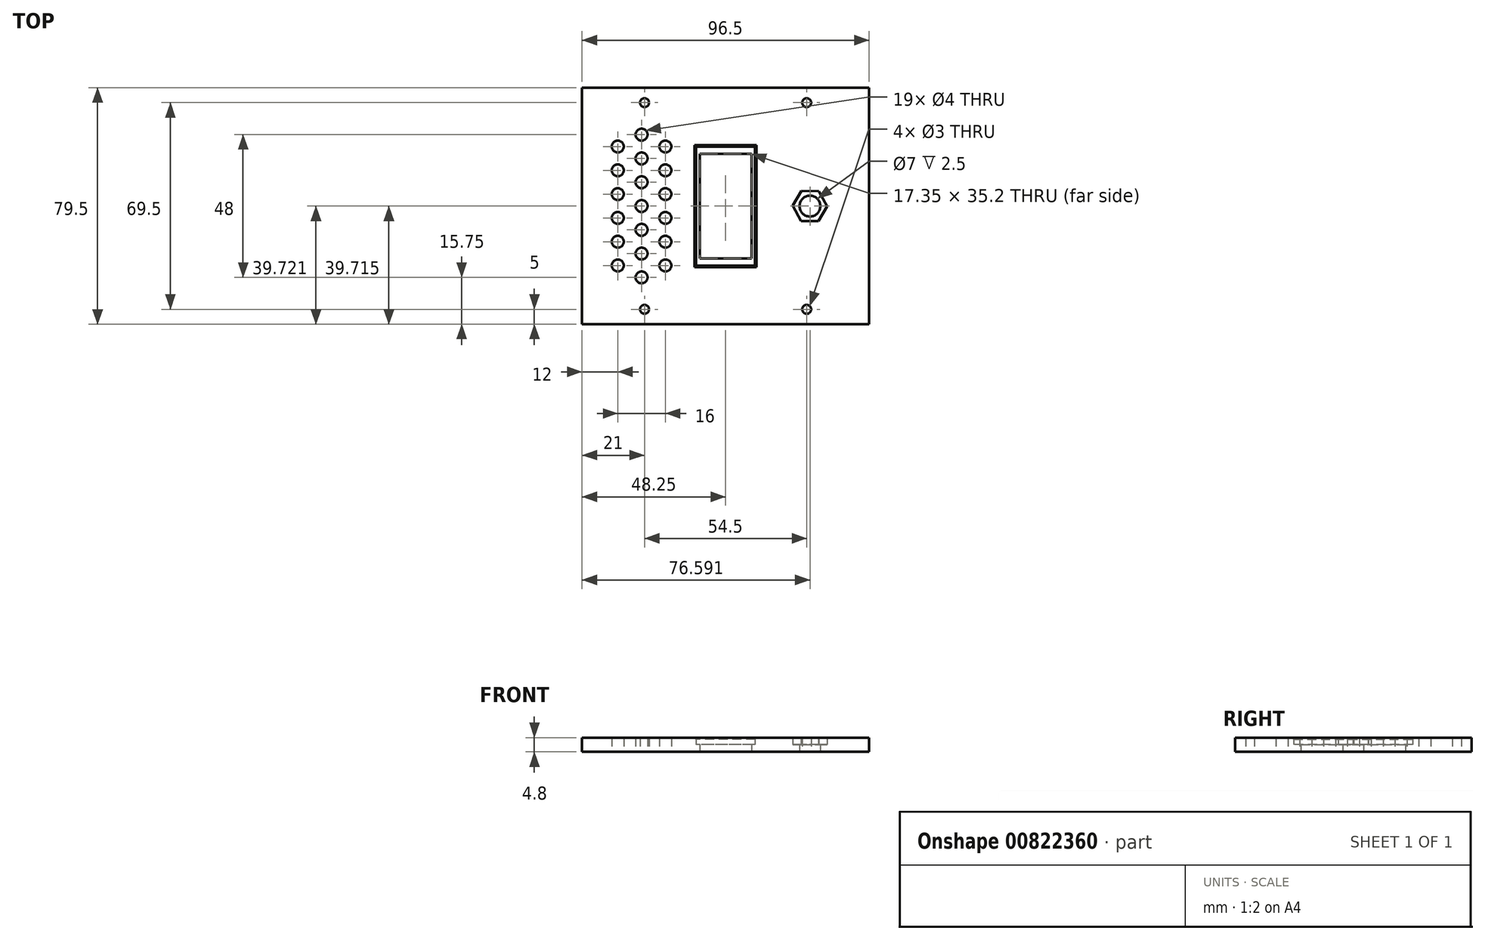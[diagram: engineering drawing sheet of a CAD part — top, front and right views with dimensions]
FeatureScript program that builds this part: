
annotation { "Feature Type Name" : "Feature", "Feature Type Description" : "" }
export const myFeature = defineFeature(function(context is Context, id is Id, definition is map)
    precondition{}
    {
        {
            var Q0;
            Q0=qCreatedBy(makeId("Top.planeOp"),FACE);
            var sketch = newSketch(context, id + "F0", { "sketchPlane" : qUnion([Q0])});
            skLineSegment(sketch, "E0.bottom", {"start": v(48.25, -39.75) * mm, "end": v(-48.25, -39.75) * mm});
            skLineSegment(sketch, "E0.top", {"start": v(48.25, 39.75) * mm, "end": v(-48.25, 39.75) * mm});
            skLineSegment(sketch, "E0.left", {"start": v(48.25, -39.75) * mm, "end": v(48.25, 39.75) * mm});
            skLineSegment(sketch, "E0.right", {"start": v(-48.25, -39.75) * mm, "end": v(-48.25, 39.75) * mm});
            skLineSegment(sketch, "E1", {"start": v(-48.25, 39.75) * mm, "end": v(-48.25, 34.75) * mm});
            skLineSegment(sketch, "E2", {"start": v(-48.25, 34.75) * mm, "end": v(48.25, 34.75) * mm, "construction": true});
            skLineSegment(sketch, "E3", {"start": v(-48.25, -39.75) * mm, "end": v(-48.25, -34.75) * mm});
            skLineSegment(sketch, "E4", {"start": v(-48.25, -34.75) * mm, "end": v(48.25, -34.75) * mm, "construction": true});
            skLineSegment(sketch, "E5", {"start": v(-48.25, -34.75) * mm, "end": v(-27.25, -34.75) * mm});
            skLineSegment(sketch, "E6", {"start": v(48.25, -34.75) * mm, "end": v(27.25, -34.75) * mm});
            skLineSegment(sketch, "E7", {"start": v(-48.25, 34.75) * mm, "end": v(-27.25, 34.75) * mm});
            skLineSegment(sketch, "E8", {"start": v(48.25, 34.75) * mm, "end": v(27.25, 34.75) * mm});
            skLineSegment(sketch, "E9", {"start": v(-28.25, -39.75) * mm, "end": v(-28.25, 39.75) * mm, "construction": true});
            skLineSegment(sketch, "E10", {"start": v(-48.25, 0) * mm, "end": v(-28.25, 0) * mm, "construction": true});
            skPoint(sketch, "E11.middle", {"position": v(-28.25, 0) * mm});
            skCircle(sketch, "E12", {"center": v(-28.25, 0) * mm, "radius": 2 * mm});
            skLineSegment(sketch, "E13", {"start": v(-28.25, 0) * mm, "end": v(-28.25, 8) * mm});
            skCircle(sketch, "E14", {"center": v(-28.25, 8) * mm, "radius": 2 * mm});
            skLineSegment(sketch, "E15", {"start": v(-28.25, 8) * mm, "end": v(-28.25, 16) * mm});
            skLineSegment(sketch, "E16", {"start": v(-28.25, 16) * mm, "end": v(-28.25, 24) * mm});
            skCircle(sketch, "E17", {"center": v(-28.25, 24) * mm, "radius": 2 * mm});
            skCircle(sketch, "E18", {"center": v(-28.25, 16) * mm, "radius": 2 * mm});
            skCircle(sketch, "E19", {"center": v(-36.25, 20) * mm, "radius": 2 * mm});
            skCircle(sketch, "E20", {"center": v(-36.25, 12) * mm, "radius": 2 * mm});
            skCircle(sketch, "E21", {"center": v(-36.25, 4) * mm, "radius": 2 * mm});
            skCircle(sketch, "E22.MirrorC", {"center": v(-36.25, -4) * mm, "radius": 2 * mm});
            skCircle(sketch, "E23.MirrorC", {"center": v(-28.25, -8) * mm, "radius": 2 * mm});
            skCircle(sketch, "E24.MirrorC", {"center": v(-36.25, -12) * mm, "radius": 2 * mm});
            skCircle(sketch, "E25.MirrorC", {"center": v(-36.25, -20) * mm, "radius": 2 * mm});
            skCircle(sketch, "E26.MirrorC", {"center": v(-28.25, -24) * mm, "radius": 2 * mm});
            skCircle(sketch, "E27.MirrorC", {"center": v(-28.25, -16) * mm, "radius": 2 * mm});
            skCircle(sketch, "E28.MirrorC", {"center": v(-20.25, 20) * mm, "radius": 2 * mm});
            skCircle(sketch, "E29.MirrorC", {"center": v(-20.25, 12) * mm, "radius": 2 * mm});
            skCircle(sketch, "E30.MirrorC", {"center": v(-20.25, 4) * mm, "radius": 2 * mm});
            skCircle(sketch, "E31.MirrorC", {"center": v(-20.25, -4) * mm, "radius": 2 * mm});
            skCircle(sketch, "E32.MirrorC", {"center": v(-20.25, -12) * mm, "radius": 2 * mm});
            skCircle(sketch, "E33.MirrorC", {"center": v(-20.25, -20) * mm, "radius": 2 * mm});
            skLineSegment(sketch, "E34", {"start": v(48.25, 0) * mm, "end": v(28.25, 0) * mm});
            skPoint(sketch, "E35.middle", {"position": v(28.34, -0.03) * mm});
            skCircle(sketch, "E36.cCircle", {"center": v(28.34, -0.03) * mm, "radius": 5.83 * mm, "construction": true});
            skLineSegment(sketch, "E36.0", {"start": v(25.33, -5.03) * mm, "end": v(22.51, 0.08) * mm});
            skLineSegment(sketch, "E36.1", {"start": v(22.51, 0.08) * mm, "end": v(25.52, 5.07) * mm});
            skLineSegment(sketch, "E36.2", {"start": v(25.52, 5.07) * mm, "end": v(31.35, 4.97) * mm});
            skLineSegment(sketch, "E36.3", {"start": v(31.35, 4.97) * mm, "end": v(34.17, -0.13) * mm});
            skLineSegment(sketch, "E36.4", {"start": v(34.17, -0.13) * mm, "end": v(31.16, -5.13) * mm});
            skLineSegment(sketch, "E36.5", {"start": v(31.16, -5.13) * mm, "end": v(25.33, -5.03) * mm});
            skPoint(sketch, "E37", {"position": v(0, -0.04) * mm});
            skLineSegment(sketch, "E38.bottom", {"start": v(9.9, 19.96) * mm, "end": v(-9.9, 19.96) * mm});
            skLineSegment(sketch, "E38.top", {"start": v(9.9, -20.04) * mm, "end": v(-9.9, -20.04) * mm});
            skLineSegment(sketch, "E38.left", {"start": v(9.9, 19.96) * mm, "end": v(9.9, -20.04) * mm});
            skLineSegment(sketch, "E38.right", {"start": v(-9.9, 19.96) * mm, "end": v(-9.9, -20.04) * mm});
            skLineSegment(sketch, "E39", {"start": v(0, -0.04) * mm, "end": v(0, -20.04) * mm, "construction": true});
            skLineSegment(sketch, "E40", {"start": v(0, -0.04) * mm, "end": v(9.9, -0.04) * mm, "construction": true});
            skLineSegment(sketch, "E41", {"start": v(0, -0.04) * mm, "end": v(0, -14.29) * mm, "construction": true});
            skLineSegment(sketch, "E42", {"start": v(0, -0.04) * mm, "end": v(6.75, -0.04) * mm, "construction": true});
            skLineSegment(sketch, "E43.bottom", {"start": v(8.67, -17.64) * mm, "end": v(-8.68, -17.64) * mm});
            skLineSegment(sketch, "E43.top", {"start": v(8.68, 17.56) * mm, "end": v(-8.67, 17.56) * mm});
            skLineSegment(sketch, "E43.left", {"start": v(8.68, -17.64) * mm, "end": v(8.68, 17.56) * mm});
            skLineSegment(sketch, "E43.right", {"start": v(-8.68, -17.64) * mm, "end": v(-8.67, 17.56) * mm});
            skSolve(sketch);
        }
        {
            var Q0;
            Q0=makeQuery(id+"F0.imprint","IMPRINT",FACE,{"disambiguationData":[TD([[makeQuery(id+"F0.imprint","IMPRINT",EDGE,{"derivedFrom":sQuery(id+"F0.wireOp",EDGE,"E0.bottom")}),-1.0]])]});
            extrude(context, id + "F1", {"entities" : qUnion([Q0]), "depth" : 4.8 * mm, "offsetDistance" : 25 * mm});
        }
        {
            var Q0;
            Q0=sQuery(id+"F0.wireOp",VERTEX,"E7.end");
            var Q1;
            Q1=sQuery(id+"F0.wireOp",VERTEX,"E8.end");
            var Q2;
            Q2=sQuery(id+"F0.wireOp",VERTEX,"E6.end");
            var Q3;
            Q3=sQuery(id+"F0.wireOp",VERTEX,"E5.end");
            var Q4;
            Q4=makeQuery(id+"F1.opExtrude","SWEPT_BODY",BODY,{"disambiguationData":[OSD([sQuery(id+"F0.wireOp",EDGE,"E0.bottom"),sQuery(id+"F0.wireOp",EDGE,"E0.top"),sQuery(id+"F0.wireOp",EDGE,"E0.left"),sQuery(id+"F0.wireOp",EDGE,"E0.right"),sQuery(id+"F0.wireOp",EDGE,"E1"),sQuery(id+"F0.wireOp",EDGE,"E3")])]});
            hole(context, id + "F2", {"style" : HoleStyle.C_SINK, "endStyle" : HoleEndStyle.BLIND, "oppositeDirection" : true, "holeDiameter" : 3 * mm, "cSinkDiameter" : 3 * mm, "cSinkAngle" : 90 * degree, "majorDiameter" : 5 * mm, "holeDepth" : 5 * mm, "isTappedThrough" : true, "tappedDepth" : 12 * mm, "tapClearance" : 3, "locations" : qUnion([Q0, Q1, Q2, Q3]), "scope" : qUnion([Q4])});
        }
        {
            var Q0;
            Q0=makeQuery(id+"F0.imprint","IMPRINT",FACE,{"disambiguationData":[TD([[makeQuery(id+"F0.imprint","IMPRINT",EDGE,{"derivedFrom":sQuery(id+"F0.wireOp",EDGE,"QwRBpnaT-Zvc7-lyGs-djqg-7ZUYDCY1tUwC.bottom")}),1.0]])]});
            var Q1;
            Q1=makeQuery(id+"F0.imprint","IMPRINT",FACE,{"disambiguationData":[TD([[makeQuery(id+"F0.imprint","IMPRINT",EDGE,{"derivedFrom":sQuery(id+"F0.wireOp",EDGE,"E38.bottom")}),1.0]])]});
            extrude(context, id + "F3", {"entities" : qUnion([Q0, Q1]), "operationType" : NewBodyOperationType.ADD, "depth" : 2.5 * mm, "offsetDistance" : 25 * mm});
        }
        {
            var Q0;
            Q0=makeQuery(id+"F0.imprint","IMPRINT",FACE,{"disambiguationData":[TD([[makeQuery(id+"F0.imprint","IMPRINT",EDGE,{"derivedFrom":sQuery(id+"F0.wireOp",EDGE,"24598238-bea3-4d77-90ff-679a99b3edff.0")}),-1.0]])]});
            var Q1;
            Q1=makeQuery(id+"F0.imprint","IMPRINT",FACE,{"disambiguationData":[TD([[makeQuery(id+"F0.imprint","IMPRINT",EDGE,{"derivedFrom":sQuery(id+"F0.wireOp",EDGE,"E36.0")}),-1.0]])]});
            extrude(context, id + "F4", {"entities" : qUnion([Q0, Q1]), "operationType" : NewBodyOperationType.ADD, "depth" : 2.5 * mm, "offsetDistance" : 25 * mm});
        }
        {
            var Q0;
            Q0=sQuery(id+"F0.wireOp",VERTEX,"E0.middle");
            var Q1;
            Q1=sQuery(id+"F0.wireOp",VERTEX,"E35.middle");
            var Q2;
            Q2=makeQuery(id+"F1.opExtrude","SWEPT_BODY",BODY,{"disambiguationData":[OSD([sQuery(id+"F0.wireOp",EDGE,"E0.bottom"),sQuery(id+"F0.wireOp",EDGE,"E0.top"),sQuery(id+"F0.wireOp",EDGE,"E0.left"),sQuery(id+"F0.wireOp",EDGE,"E0.right"),sQuery(id+"F0.wireOp",EDGE,"E1"),sQuery(id+"F0.wireOp",EDGE,"E3"),sQuery(id+"F0.wireOp",EDGE,"QwRBpnaT-Zvc7-lyGs-djqg-7ZUYDCY1tUwC.bottom"),sQuery(id+"F0.wireOp",EDGE,"QwRBpnaT-Zvc7-lyGs-djqg-7ZUYDCY1tUwC.top"),sQuery(id+"F0.wireOp",EDGE,"QwRBpnaT-Zvc7-lyGs-djqg-7ZUYDCY1tUwC.left"),sQuery(id+"F0.wireOp",EDGE,"QwRBpnaT-Zvc7-lyGs-djqg-7ZUYDCY1tUwC.right"),sQuery(id+"F0.wireOp",EDGE,"24598238-bea3-4d77-90ff-679a99b3edff.0"),sQuery(id+"F0.wireOp",EDGE,"24598238-bea3-4d77-90ff-679a99b3edff.1"),sQuery(id+"F0.wireOp",EDGE,"24598238-bea3-4d77-90ff-679a99b3edff.2"),sQuery(id+"F0.wireOp",EDGE,"24598238-bea3-4d77-90ff-679a99b3edff.3"),sQuery(id+"F0.wireOp",EDGE,"24598238-bea3-4d77-90ff-679a99b3edff.4"),sQuery(id+"F0.wireOp",EDGE,"24598238-bea3-4d77-90ff-679a99b3edff.5")])]});
            hole(context, id + "F5", {"style" : HoleStyle.SIMPLE, "endStyle" : HoleEndStyle.BLIND, "oppositeDirection" : true, "holeDiameter" : 7 * mm, "majorDiameter" : 5 * mm, "holeDepth" : 7 * mm, "isTappedThrough" : true, "tappedDepth" : 12 * mm, "tapClearance" : 3, "locations" : qUnion([Q0, Q1]), "scope" : qUnion([Q2])});
        }
        {
            var Q0;
            Q0=makeQuery(id+"F1.opExtrude","CAP_EDGE",EDGE,{"disambiguationData":[OSD([sQuery(id+"F0.wireOp",EDGE,"E38.right")])],"isStart":false});
            var Q1;
            Q1=makeQuery(id+"F1.opExtrude","CAP_EDGE",EDGE,{"disambiguationData":[OSD([sQuery(id+"F0.wireOp",EDGE,"E38.bottom")])],"isStart":false});
            var Q2;
            Q2=makeQuery(id+"F1.opExtrude","CAP_EDGE",EDGE,{"disambiguationData":[OSD([sQuery(id+"F0.wireOp",EDGE,"E38.left")])],"isStart":false});
            var Q3;
            Q3=makeQuery(id+"F1.opExtrude","CAP_EDGE",EDGE,{"disambiguationData":[OSD([sQuery(id+"F0.wireOp",EDGE,"E38.top")])],"isStart":false});
            chamfer(context, id + "F6", {"entities" : qUnion([Q0, Q1, Q2, Q3]), "width" : 0.5 * mm, "tangentPropagation" : true});
        }
    });
